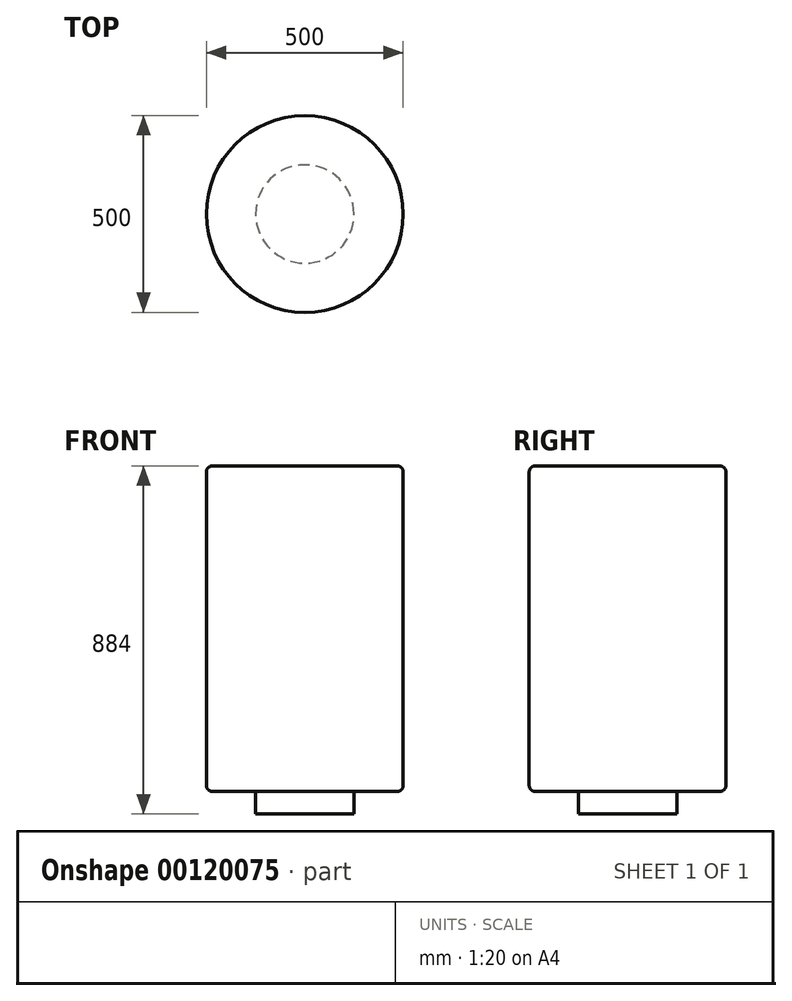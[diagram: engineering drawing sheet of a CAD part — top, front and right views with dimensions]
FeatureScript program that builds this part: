
annotation { "Feature Type Name" : "Feature", "Feature Type Description" : "" }
export const myFeature = defineFeature(function(context is Context, id is Id, definition is map)
    precondition{}
    {
        {
            var Q0;
            Q0=qCreatedBy(makeId("Top.planeOp"),FACE);
            var sketch = newSketch(context, id + "F0", { "sketchPlane" : qUnion([Q0])});
            skCircle(sketch, "E0", {"center": v(0, 0) * mm, "radius": 250 * mm});
            skCircle(sketch, "E1", {"center": v(0, 0) * mm, "radius": 125 * mm});
            skSolve(sketch);
        }
        {
            var Q0;
            Q0=makeQuery(id+"F0.imprint","IMPRINT",FACE,{"disambiguationData":[TD([[makeQuery(id+"F0.imprint","IMPRINT",EDGE,{"derivedFrom":sQuery(id+"F0.wireOp",EDGE,"E0")}),1.0]])]});
            var Q1;
            Q1=makeQuery(id+"F0.imprint","IMPRINT",FACE,{"disambiguationData":[TD([[makeQuery(id+"F0.imprint","IMPRINT",EDGE,{"derivedFrom":sQuery(id+"F0.wireOp",EDGE,"E1")}),1.0]])]});
            extrude(context, id + "F1", {"entities" : qUnion([Q0, Q1]), "depth" : 827 * mm});
        }
        {
            var Q0;
            Q0=makeQuery(id+"F0.imprint","IMPRINT",FACE,{"disambiguationData":[TD([[makeQuery(id+"F0.imprint","IMPRINT",EDGE,{"derivedFrom":sQuery(id+"F0.wireOp",EDGE,"E1")}),1.0]])]});
            extrude(context, id + "F2", {"entities" : qUnion([Q0]), "operationType" : NewBodyOperationType.ADD, "oppositeDirection" : true, "depth" : 57 * mm});
        }
        {
            var Q0;
            Q0=makeQuery(id+"F1.opExtrude","CAP_EDGE",EDGE,{"disambiguationData":[OSD([sQuery(id+"F0.wireOp",EDGE,"E0")])],"isStart":false});
            var Q1;
            Q1=makeQuery(id+"F1.opExtrude","CAP_EDGE",EDGE,{"disambiguationData":[OSD([sQuery(id+"F0.wireOp",EDGE,"E0")])],"isStart":true});
            fillet(context, id + "F3", {"entities" : qUnion([Q0, Q1]), "radius" : 15 * mm, "tangentPropagation" : true, "allowEdgeOverflow" : false});
        }
    });
